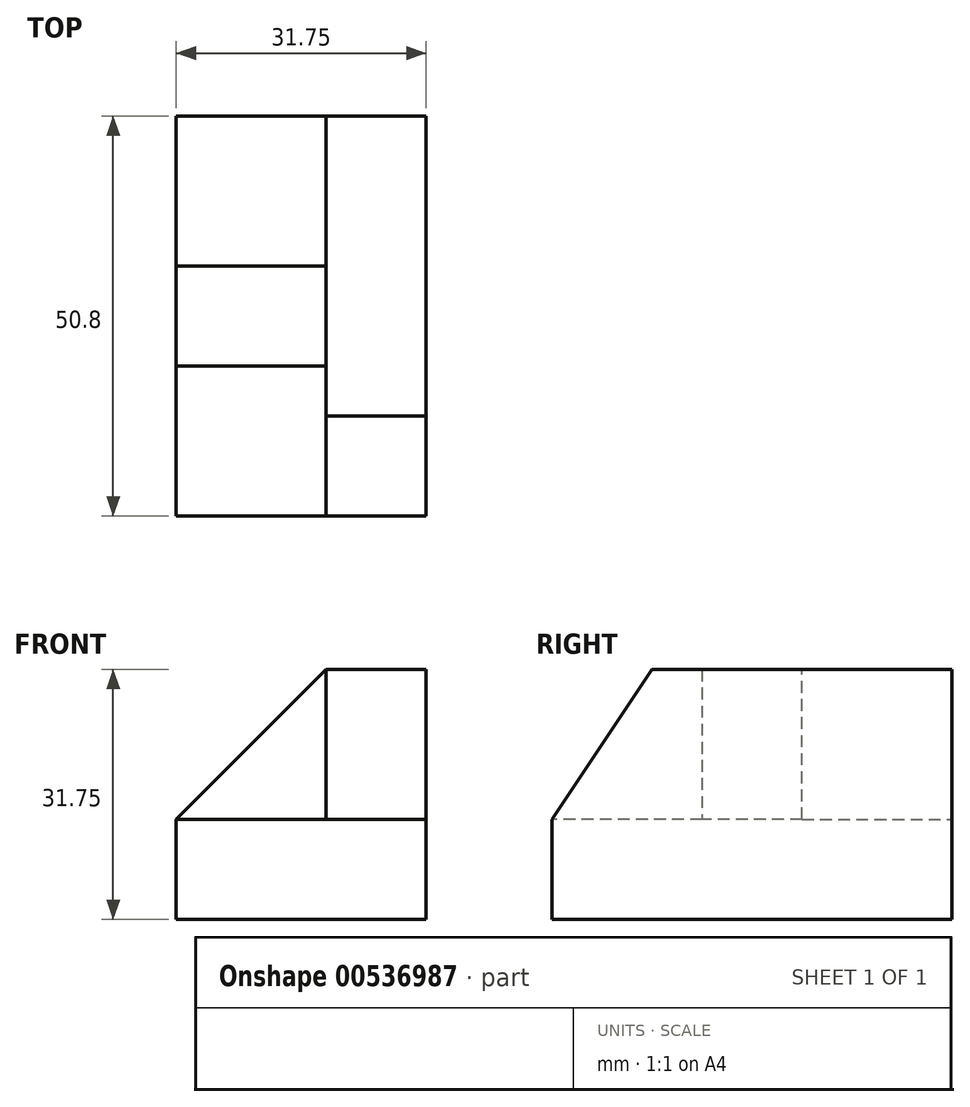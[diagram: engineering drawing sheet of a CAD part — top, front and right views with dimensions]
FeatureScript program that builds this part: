
annotation { "Feature Type Name" : "Feature", "Feature Type Description" : "" }
export const myFeature = defineFeature(function(context is Context, id is Id, definition is map)
    precondition{}
    {
        {
            var Q0;
            Q0=qCreatedBy(makeId("Front.planeOp"),FACE);
            var sketch = newSketch(context, id + "F0", { "sketchPlane" : qUnion([Q0])});
            skLineSegment(sketch, "E0", {"start": v(-55.78, 20.2) * mm, "end": v(-55.78, 51.96) * mm});
            skLineSegment(sketch, "E1", {"start": v(-55.78, 20.2) * mm, "end": v(-24.03, 20.2) * mm});
            skLineSegment(sketch, "E2", {"start": v(-24.03, 20.2) * mm, "end": v(-24.03, 51.96) * mm});
            skLineSegment(sketch, "E3", {"start": v(-24.03, 51.96) * mm, "end": v(-55.78, 51.96) * mm});
            skSolve(sketch);
        }
        {
            var Q0;
            Q0=makeQuery(id+"F0.imprint","IMPRINT",FACE,{"disambiguationData":[TD([[makeQuery(id+"F0.imprint","IMPRINT",EDGE,{"derivedFrom":sQuery(id+"F0.wireOp",EDGE,"E0")}),-1.0]])]});
            extrude(context, id + "F1", {"entities" : qUnion([Q0]), "depth" : 50.8 * mm, "offsetDistance" : 25.4 * mm});
        }
        {
            var Q0;
            Q0=makeQuery(id+"F1.opExtrude","CAP_FACE",FACE,{"disambiguationData":[OSD([sQuery(id+"F0.wireOp",EDGE,"E0"),sQuery(id+"F0.wireOp",EDGE,"E1"),sQuery(id+"F0.wireOp",EDGE,"E2"),sQuery(id+"F0.wireOp",EDGE,"E3")])],"isStart":false});
            var sketch = newSketch(context, id + "F2", { "sketchPlane" : qUnion([Q0])});
            skLineSegment(sketch, "E4", {"start": v(-36.73, 51.96) * mm, "end": v(-36.73, 32.9) * mm});
            skLineSegment(sketch, "E5", {"start": v(-36.73, 32.9) * mm, "end": v(-55.78, 32.9) * mm});
            skSolve(sketch);
        }
        {
            var Q0;
            {var subQ0=sQuery(id+"F2.wireOp",EDGE,"E4");Q0=makeQuery(id+"F2.imprint","IMPRINT",FACE,{"disambiguationData":[TD([[makeQuery(id+"F2.imprint","IMPRINT",EDGE,{"derivedFrom":subQ0}),-1.0]])]});}
            extrude(context, id + "F3", {"entities" : qUnion([Q0]), "operationType" : NewBodyOperationType.REMOVE, "oppositeDirection" : true, "depth" : 19.05 * mm, "offsetDistance" : 25.4 * mm});
        }
        {
            var Q0;
            Q0=makeQuery(id+"F1.opExtrude","CAP_FACE",FACE,{"disambiguationData":[OSD([sQuery(id+"F0.wireOp",EDGE,"E0"),sQuery(id+"F0.wireOp",EDGE,"E1"),sQuery(id+"F0.wireOp",EDGE,"E2"),sQuery(id+"F0.wireOp",EDGE,"E3")])],"isStart":true});
            var sketch = newSketch(context, id + "F4", { "sketchPlane" : qUnion([Q0])});
            skLineSegment(sketch, "E6", {"start": v(36.73, 51.96) * mm, "end": v(36.73, 32.9) * mm});
            skLineSegment(sketch, "E7", {"start": v(36.73, 32.9) * mm, "end": v(55.78, 32.9) * mm});
            skSolve(sketch);
        }
        {
            var Q0;
            {var subQ0=sQuery(id+"F4.wireOp",EDGE,"E6");Q0=makeQuery(id+"F4.imprint","IMPRINT",FACE,{"disambiguationData":[TD([[makeQuery(id+"F4.imprint","IMPRINT",EDGE,{"derivedFrom":subQ0}),1.0]])]});}
            extrude(context, id + "F5", {"entities" : qUnion([Q0]), "operationType" : NewBodyOperationType.REMOVE, "oppositeDirection" : true, "depth" : 19.05 * mm, "offsetDistance" : 25.4 * mm});
        }
        {
            var Q0;
            Q0=makeQuery(id+"F3.boolean.opBoolean","COPY",FACE,{"derivedFrom":makeQuery(id+"F3.opExtrude","CAP_FACE",FACE,{"disambiguationData":[OSD([sQuery(id+"F0.wireOp",EDGE,"E0"),sQuery(id+"F0.wireOp",EDGE,"E3"),sQuery(id+"F2.wireOp",EDGE,"E4"),sQuery(id+"F2.wireOp",EDGE,"E5")])],"isStart":false})});
            var sketch = newSketch(context, id + "F6", { "sketchPlane" : qUnion([Q0])});
            skLineSegment(sketch, "E8", {"start": v(-36.73, 51.96) * mm, "end": v(-55.78, 32.9) * mm});
            skSolve(sketch);
        }
        {
            var Q0;
            Q0=makeQuery(id+"F6.imprint","IMPRINT",FACE,{"disambiguationData":[TD([[makeQuery(id+"F6.imprint","IMPRINT",EDGE,{"derivedFrom":sQuery(id+"F6.wireOp",EDGE,"E8")}),-1.0]])]});
            extrude(context, id + "F7", {"entities" : qUnion([Q0]), "operationType" : NewBodyOperationType.REMOVE, "endBound" : BoundingType.THROUGH_ALL, "oppositeDirection" : true, "depth" : 25.4 * mm, "offsetDistance" : 25.4 * mm});
        }
        {
            var Q0;
            Q0=makeQuery(id+"F3.boolean.opBoolean","COPY",FACE,{"derivedFrom":makeQuery(id+"F3.opExtrude","SWEPT_FACE",FACE,{"disambiguationData":[OSD([sQuery(id+"F2.wireOp",EDGE,"E4")])]})});
            var sketch = newSketch(context, id + "F8", { "sketchPlane" : qUnion([Q0])});
            skLineSegment(sketch, "E9", {"start": v(38.1, 51.96) * mm, "end": v(50.8, 32.9) * mm});
            skSolve(sketch);
        }
        {
            var Q0;
            {var subQ0=sQuery(id+"F8.wireOp",EDGE,"E9");Q0=makeQuery(id+"F8.imprint","IMPRINT",FACE,{"disambiguationData":[TD([[makeQuery(id+"F8.imprint","IMPRINT",EDGE,{"derivedFrom":subQ0}),1.0]])]});}
            extrude(context, id + "F9", {"entities" : qUnion([Q0]), "operationType" : NewBodyOperationType.REMOVE, "endBound" : BoundingType.THROUGH_ALL, "oppositeDirection" : true, "depth" : 25.4 * mm, "offsetDistance" : 25.4 * mm});
        }
    });
